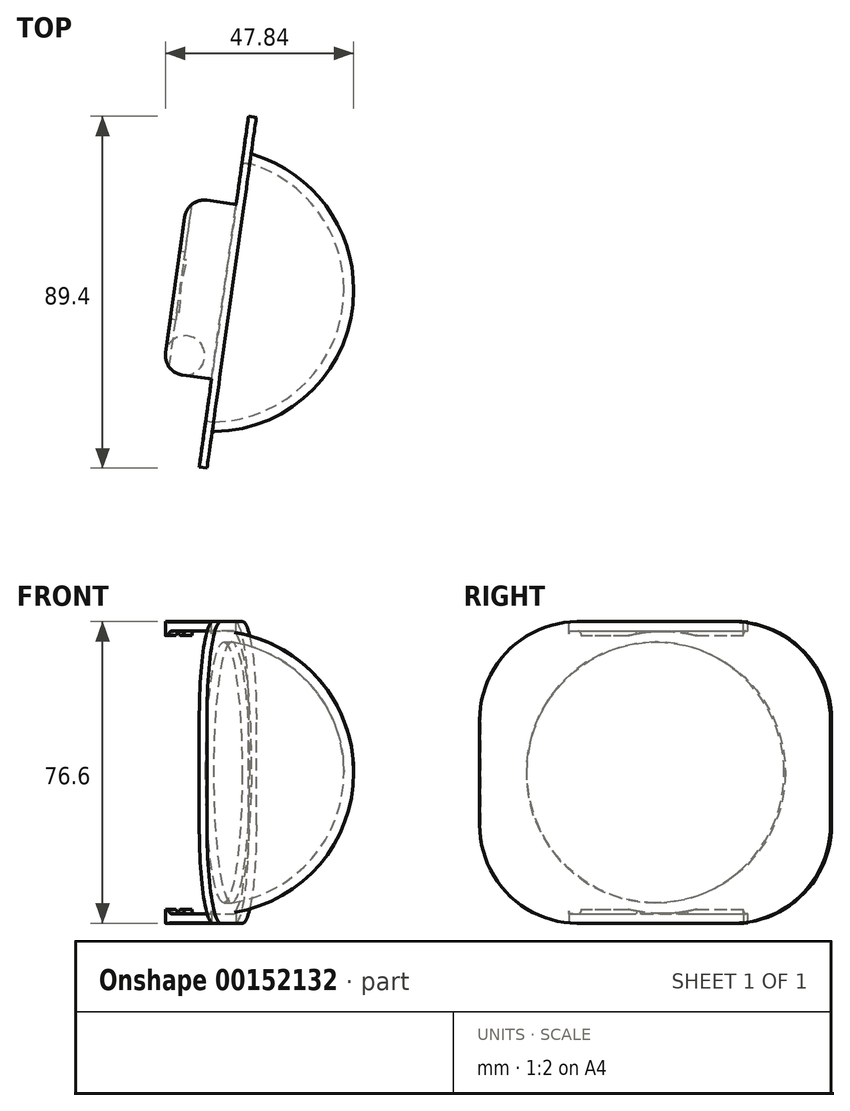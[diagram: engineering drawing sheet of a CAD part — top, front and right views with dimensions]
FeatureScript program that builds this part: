
annotation { "Feature Type Name" : "Feature", "Feature Type Description" : "" }
export const myFeature = defineFeature(function(context is Context, id is Id, definition is map)
    precondition{}
    {
        {
            var Q0;
            Q0=qCreatedBy(makeId("Front.planeOp"),FACE);
            var sketch = newSketch(context, id + "F0", { "sketchPlane" : qUnion([Q0])});
            skArc(sketch, "E0", {"start": v(36, 0) * mm, "mid": v(25.46, 25.46) * mm, "end": v(0, 36) * mm});
            skLineSegment(sketch, "E1", {"start": v(0, 0) * mm, "end": v(36, 0) * mm});
            skLineSegment(sketch, "E2", {"start": v(0, 36) * mm, "end": v(0, 0) * mm});
            skLineSegment(sketch, "E3", {"start": v(0, 0) * mm, "end": v(-36.2, 0) * mm});
            skSolve(sketch);
        }
        {
            var Q0;
            Q0=makeQuery(id+"F0.imprint","IMPRINT",FACE,{"disambiguationData":[TD([[makeQuery(id+"F0.imprint","IMPRINT",EDGE,{"derivedFrom":sQuery(id+"F0.wireOp",EDGE,"E0")}),1.0]])]});
            var Q1;
            Q1=sQuery(id+"F0.wireOp",EDGE,"E3");
            revolve(context, id + "F1", {"entities" : qUnion([Q0]), "axis" : qUnion([Q1]), "revolveType" : RevolveType.FULL});
        }
        {
            var Q0;
            Q0=qCreatedBy(makeId("Top.planeOp"),FACE);
            var sketch = newSketch(context, id + "F2", { "sketchPlane" : qUnion([Q0])});
            skLineSegment(sketch, "E4", {"start": v(0, -36.24) * mm, "end": v(10.22, 36.47) * mm});
            skLineSegment(sketch, "E5", {"start": v(10.22, 36.47) * mm, "end": v(0, 36.47) * mm});
            skLineSegment(sketch, "E6", {"start": v(0, 36.47) * mm, "end": v(0, -36.24) * mm});
            skSolve(sketch);
        }
        {
            var Q0;
            Q0=makeQuery(id+"F1.opRevolve","SWEPT_FACE",FACE,{"disambiguationData":[OSD([sQuery(id+"F0.wireOp",EDGE,"E2")])]});
            shell(context, id + "F3", {"entities" : qUnion([Q0]), "thickness" : 2.5 * mm});
        }
        {
            var Q0;
            Q0 = qSketchRegion(id + "F2", true);
            extrude(context, id + "F4", {"entities" : qUnion([Q0]), "operationType" : NewBodyOperationType.REMOVE, "endBound" : BoundingType.SYMMETRIC, "oppositeDirection" : true, "depth" : 60 * mm});
        }
        {
            var Q0;
            Q0=makeQuery(id+"F4.boolean.opBoolean","COPY",FACE,{"derivedFrom":makeQuery(id+"F4.opExtrude","SWEPT_FACE",FACE,{"disambiguationData":[OSD([sQuery(id+"F2.wireOp",EDGE,"E4")])]})});
            var sketch = newSketch(context, id + "F5", { "sketchPlane" : qUnion([Q0])});
            skLineSegment(sketch, "E7.bottom", {"start": v(45, -38.3) * mm, "end": v(-45, -38.3) * mm});
            skLineSegment(sketch, "E7.top", {"start": v(45, 38.3) * mm, "end": v(-45, 38.3) * mm});
            skLineSegment(sketch, "E7.left", {"start": v(45, -38.3) * mm, "end": v(45, 38.3) * mm});
            skLineSegment(sketch, "E7.right", {"start": v(-45, -38.3) * mm, "end": v(-45, 38.3) * mm});
            skPoint(sketch, "E7.middle", {"position": v(0, 0) * mm});
            skCircle(sketch, "E8.0", {"center": v(0, 0) * mm, "radius": 33.12 * mm});
            skSolve(sketch);
        }
        {
            var Q0;
            Q0 = qSketchRegion(id + "F5", true);
            extrude(context, id + "F6", {"entities" : qUnion([Q0]), "operationType" : NewBodyOperationType.ADD, "depth" : 2 * mm});
        }
        {
            var Q0;
            Q0=makeQuery(id+"F6.opExtrude","CAP_FACE",FACE,{"disambiguationData":[OSD([sQuery(id+"F5.wireOp",EDGE,"E7.bottom"),sQuery(id+"F5.wireOp",EDGE,"E7.top"),sQuery(id+"F5.wireOp",EDGE,"E7.left"),sQuery(id+"F5.wireOp",EDGE,"E7.right"),sQuery(id+"F5.wireOp",EDGE,"E8.0")])],"isStart":false});
            var sketch = newSketch(context, id + "F7", { "sketchPlane" : qUnion([Q0])});
            skLineSegment(sketch, "E9.bottom", {"start": v(22.4, 34.8) * mm, "end": v(-22.4, 34.8) * mm});
            skLineSegment(sketch, "E9.top", {"start": v(22.4, 41.8) * mm, "end": v(-22.4, 41.8) * mm});
            skLineSegment(sketch, "E9.left", {"start": v(22.4, 34.8) * mm, "end": v(22.4, 41.8) * mm});
            skLineSegment(sketch, "E9.right", {"start": v(-22.4, 34.8) * mm, "end": v(-22.4, 41.8) * mm});
            skPoint(sketch, "E9.middle", {"position": v(0, 38.3) * mm});
            skLineSegment(sketch, "E10.MirrorCS", {"start": v(-22.4, -34.8) * mm, "end": v(-22.4, -41.8) * mm});
            skLineSegment(sketch, "E11.MirrorCS", {"start": v(22.4, -34.8) * mm, "end": v(22.4, -41.8) * mm});
            skLineSegment(sketch, "E12.MirrorCS", {"start": v(22.4, -41.8) * mm, "end": v(-22.4, -41.8) * mm});
            skLineSegment(sketch, "E13.MirrorCS", {"start": v(22.4, -34.8) * mm, "end": v(-22.4, -34.8) * mm});
            skPoint(sketch, "E14.MirrorP", {"position": v(0, -38.3) * mm});
            skSolve(sketch);
        }
        {
            var Q0;
            {var subQ0=sQuery(id+"F7.wireOp",EDGE,"E9.bottom");Q0=makeQuery(id+"F7.imprint","IMPRINT",FACE,{"disambiguationData":[TD([[makeQuery(id+"F7.imprint","IMPRINT",EDGE,{"derivedFrom":subQ0}),-1.0]])]});}
            var Q1;
            {var subQ0=sQuery(id+"F7.wireOp",EDGE,"E13.MirrorCS");Q1=makeQuery(id+"F7.imprint","IMPRINT",FACE,{"disambiguationData":[TD([[makeQuery(id+"F7.imprint","IMPRINT",EDGE,{"derivedFrom":subQ0}),1.0]])]});}
            extrude(context, id + "F8", {"entities" : qUnion([Q0, Q1]), "operationType" : NewBodyOperationType.ADD, "depth" : 12.5 * mm});
        }
        {
            var Q0;
            Q0=makeQuery(id+"F8.opExtrude","CAP_EDGE",EDGE,{"disambiguationData":[OSD([sQuery(id+"F7.wireOp",EDGE,"E9.right")])],"isStart":true});
            var Q1;
            Q1=makeQuery(id+"F8.opExtrude","CAP_EDGE",EDGE,{"disambiguationData":[OSD([sQuery(id+"F7.wireOp",EDGE,"E9.right")])],"isStart":false});
            var Q2;
            Q2=makeQuery(id+"F8.opExtrude","CAP_EDGE",EDGE,{"disambiguationData":[OSD([sQuery(id+"F7.wireOp",EDGE,"E9.left")])],"isStart":false});
            var Q3;
            Q3=makeQuery(id+"F8.opExtrude","CAP_EDGE",EDGE,{"disambiguationData":[OSD([sQuery(id+"F7.wireOp",EDGE,"E9.left")])],"isStart":true});
            var Q4;
            Q4=makeQuery(id+"F8.opExtrude","CAP_EDGE",EDGE,{"disambiguationData":[OSD([sQuery(id+"F7.wireOp",EDGE,"E11.MirrorCS")])],"isStart":true});
            var Q5;
            Q5=makeQuery(id+"F8.opExtrude","CAP_EDGE",EDGE,{"disambiguationData":[OSD([sQuery(id+"F7.wireOp",EDGE,"E11.MirrorCS")])],"isStart":false});
            var Q6;
            Q6=makeQuery(id+"F8.opExtrude","CAP_EDGE",EDGE,{"disambiguationData":[OSD([sQuery(id+"F7.wireOp",EDGE,"E10.MirrorCS")])],"isStart":false});
            var Q7;
            Q7=makeQuery(id+"F8.opExtrude","CAP_EDGE",EDGE,{"disambiguationData":[OSD([sQuery(id+"F7.wireOp",EDGE,"E10.MirrorCS")])],"isStart":true});
            fillet(context, id + "F9", {"entities" : qUnion([Q0, Q1, Q2, Q3, Q4, Q5, Q6, Q7]), "radius" : 5 * mm, "tangentPropagation" : true, "allowEdgeOverflow" : false});
        }
        {
            var Q0;
            Q0=makeQuery(id+"F6.opExtrude","SWEPT_EDGE",EDGE,{"disambiguationData":[OSD([sQuery(id+"F5.wireOp",EDGE,"E7.top"),sQuery(id+"F5.wireOp",EDGE,"E7.right")])]});
            var Q1;
            Q1=makeQuery(id+"F6.opExtrude","SWEPT_EDGE",EDGE,{"disambiguationData":[OSD([sQuery(id+"F5.wireOp",EDGE,"E7.bottom"),sQuery(id+"F5.wireOp",EDGE,"E7.right")])]});
            var Q2;
            Q2=makeQuery(id+"F6.opExtrude","SWEPT_EDGE",EDGE,{"disambiguationData":[OSD([sQuery(id+"F5.wireOp",EDGE,"E7.bottom"),sQuery(id+"F5.wireOp",EDGE,"E7.left")])]});
            var Q3;
            Q3=makeQuery(id+"F6.opExtrude","SWEPT_EDGE",EDGE,{"disambiguationData":[OSD([sQuery(id+"F5.wireOp",EDGE,"E7.top"),sQuery(id+"F5.wireOp",EDGE,"E7.left")])]});
            fillet(context, id + "F10", {"entities" : qUnion([Q0, Q1, Q2, Q3]), "radius" : 25 * mm, "tangentPropagation" : true, "allowEdgeOverflow" : false});
        }
        {
            var Q0;
            Q0=makeQuery(id+"F8.opExtrude","SWEPT_FACE",FACE,{"disambiguationData":[OSD([sQuery(id+"F7.wireOp",EDGE,"E9.right")])]});
            var sketch = newSketch(context, id + "F11", { "sketchPlane" : qUnion([Q0])});
            skLineSegment(sketch, "E15.bottom", {"start": v(-3.04, -35.9) * mm, "end": v(8.06, -35.9) * mm});
            skLineSegment(sketch, "E15.top", {"start": v(-3.04, 35.9) * mm, "end": v(8.06, 35.9) * mm});
            skLineSegment(sketch, "E15.left", {"start": v(-3.04, -35.9) * mm, "end": v(-3.04, 35.9) * mm});
            skLineSegment(sketch, "E15.right", {"start": v(8.06, -35.9) * mm, "end": v(8.06, 35.9) * mm});
            skPoint(sketch, "E15.middle", {"position": v(2.5, 0) * mm});
            skSolve(sketch);
        }
        {
            var Q0;
            Q0 = qSketchRegion(id + "F11", true);
            extrude(context, id + "F12", {"entities" : qUnion([Q0]), "operationType" : NewBodyOperationType.REMOVE, "endBound" : BoundingType.SYMMETRIC, "oppositeDirection" : true, "depth" : 100 * mm});
        }
        {
            var Q0;
            Q0=makeQuery(id+"F12.boolean.opBoolean","COPY",EDGE,{"derivedFrom":makeQuery(id+"F12.opExtrude","SWEPT_EDGE",EDGE,{"disambiguationData":[OSD([sQuery(id+"F11.wireOp",EDGE,"E15.top"),sQuery(id+"F11.wireOp",EDGE,"E15.right")])]})});
            var Q1;
            Q1=makeQuery(id+"F12.boolean.opBoolean","COPY",EDGE,{"derivedFrom":makeQuery(id+"F12.opExtrude","SWEPT_EDGE",EDGE,{"disambiguationData":[OSD([sQuery(id+"F11.wireOp",EDGE,"E15.bottom"),sQuery(id+"F11.wireOp",EDGE,"E15.right")])]})});
            fillet(context, id + "F13", {"entities" : qUnion([Q0, Q1]), "radius" : .65 * mm, "tangentPropagation" : true, "allowEdgeOverflow" : false});
        }
        {
            var Q0;
            Q0=makeQuery(id+"F6.boolean.opBoolean","SPLIT",FACE,{"disambiguationData":[TD([makeQuery(id+"F6.opExtrude","CAP_FACE",FACE,{"disambiguationData":[OSD([sQuery(id+"F5.wireOp",EDGE,"E7.bottom"),sQuery(id+"F5.wireOp",EDGE,"E7.top"),sQuery(id+"F5.wireOp",EDGE,"E7.left"),sQuery(id+"F5.wireOp",EDGE,"E7.right"),sQuery(id+"F5.wireOp",EDGE,"E8.0")])],"isStart":true})])],"derivedFrom":makeQuery(id+"F1.opRevolve","SWEPT_FACE",FACE,{"disambiguationData":[OSD([sQuery(id+"F0.wireOp",EDGE,"E0")])]})});
            var Q1;
            Q1=makeQuery(id+"F12.boolean.opBoolean","COPY",EDGE,{"derivedFrom":makeQuery(id+"F12.opExtrude","SWEPT_EDGE",EDGE,{"disambiguationData":[OSD([sQuery(id+"F11.wireOp",EDGE,"E15.bottom"),sQuery(id+"F11.wireOp",EDGE,"E15.left")])]})});
            var Q2;
            Q2=makeQuery(id+"F12.boolean.opBoolean","COPY",EDGE,{"derivedFrom":makeQuery(id+"F12.opExtrude","SWEPT_EDGE",EDGE,{"disambiguationData":[OSD([sQuery(id+"F11.wireOp",EDGE,"E15.top"),sQuery(id+"F11.wireOp",EDGE,"E15.left")])]})});
            fillet(context, id + "F14", {"entities" : qUnion([Q0, Q1, Q2]), "radius" : .7 * mm, "tangentPropagation" : true, "allowEdgeOverflow" : false});
        }
    });
